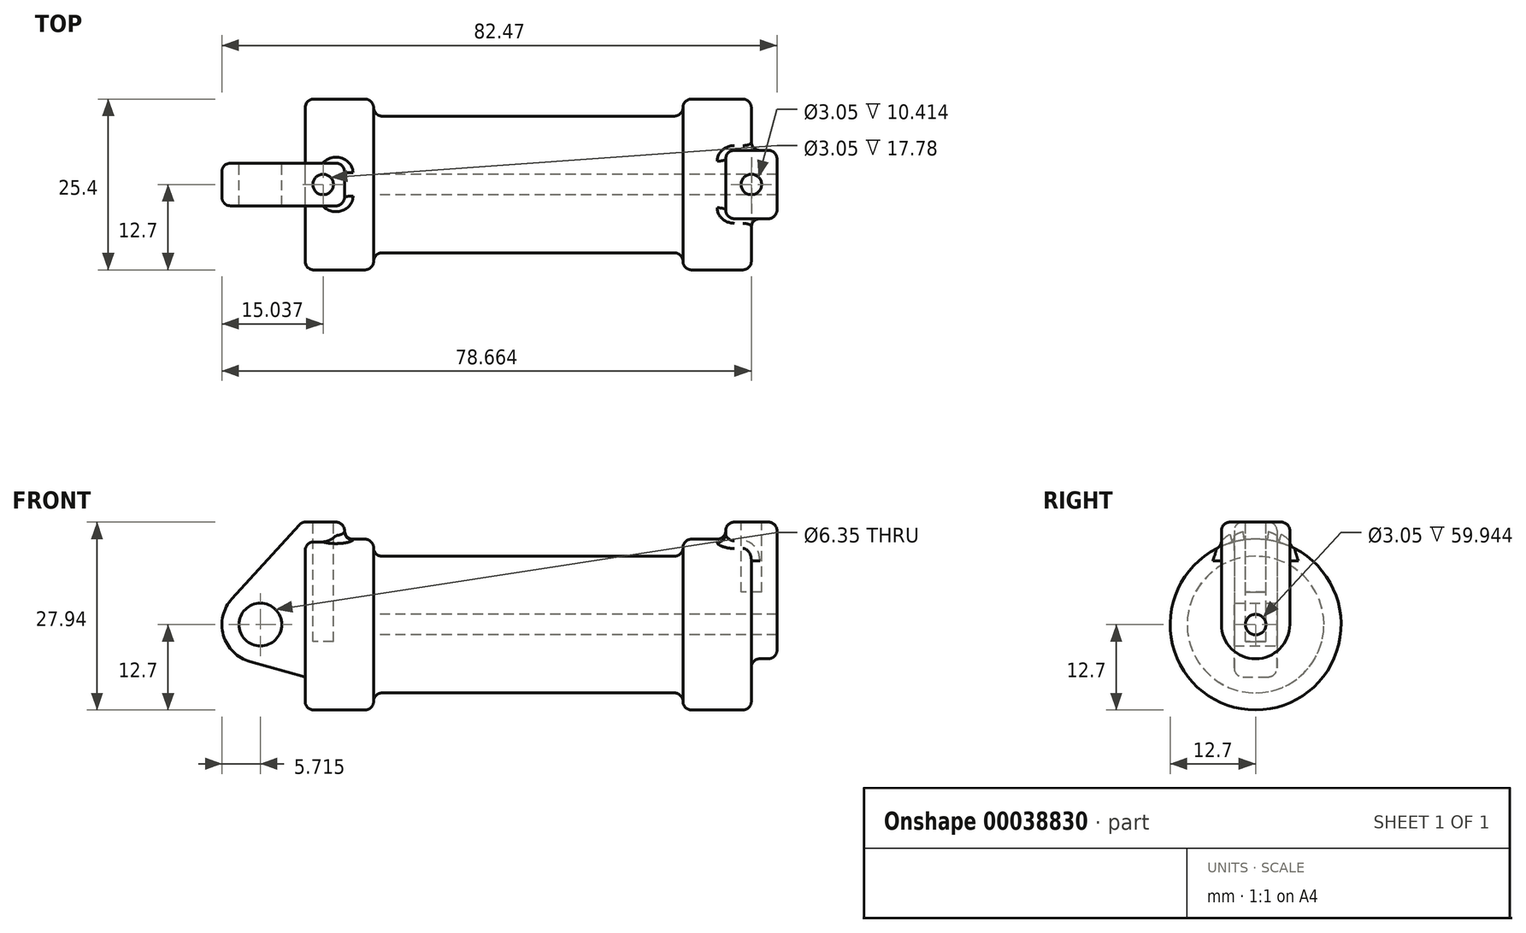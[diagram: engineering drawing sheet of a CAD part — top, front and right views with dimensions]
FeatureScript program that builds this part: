
annotation { "Feature Type Name" : "Feature", "Feature Type Description" : "" }
export const myFeature = defineFeature(function(context is Context, id is Id, definition is map)
    precondition{}
    {
        {
            var Q0;
            Q0=qCreatedBy(makeId("Front.planeOp"),FACE);
            var sketch = newSketch(context, id + "F0", { "sketchPlane" : qUnion([Q0])});
            skLineSegment(sketch, "E0", {"start": v(0, 0) * mm, "end": v(0, 12.7) * mm});
            skLineSegment(sketch, "E1", {"start": v(0, 12.7) * mm, "end": v(10.16, 12.7) * mm});
            skLineSegment(sketch, "E2", {"start": v(10.16, 12.7) * mm, "end": v(10.16, 10.16) * mm});
            skLineSegment(sketch, "E3", {"start": v(10.16, 10.16) * mm, "end": v(56.13, 10.16) * mm});
            skLineSegment(sketch, "E4", {"start": v(56.13, 10.16) * mm, "end": v(56.13, 12.7) * mm});
            skLineSegment(sketch, "E5", {"start": v(56.13, 12.7) * mm, "end": v(66.3, 12.7) * mm});
            skLineSegment(sketch, "E6", {"start": v(66.3, 12.7) * mm, "end": v(66.3, 0) * mm});
            skLineSegment(sketch, "E7", {"start": v(66.3, 0) * mm, "end": v(0, 0) * mm});
            skLineSegment(sketch, "E8", {"start": v(5.84, 15.24) * mm, "end": v(-0.5, 15.24) * mm});
            skLineSegment(sketch, "E9", {"start": v(-0.5, 15.24) * mm, "end": v(-10.88, 3.85) * mm});
            skLineSegment(sketch, "E10", {"start": v(0, 0) * mm, "end": v(-6.65, 0) * mm});
            skCircle(sketch, "E11", {"center": v(-6.65, 0) * mm, "radius": 5.72 * mm});
            skCircle(sketch, "E12", {"center": v(-6.65, 0) * mm, "radius": 3.18 * mm});
            skLineSegment(sketch, "E13", {"start": v(5.84, 15.24) * mm, "end": v(5.84, -9.4) * mm});
            skLineSegment(sketch, "E14", {"start": v(5.84, -9.4) * mm, "end": v(-8.18, -5.5) * mm});
            skSolve(sketch);
        }
        {
            var Q0;
            {var subQ6=sQuery(id+"F0.wireOp",EDGE,"E2");Q0=makeQuery(id+"F0.imprint","IMPRINT",FACE,{"disambiguationData":[TD([[makeQuery(id+"F0.imprint","IMPRINT",EDGE,{"derivedFrom":subQ6}),-1.0]])]});}
            var Q1;
            {var subQ5=sQuery(id+"F0.wireOp",EDGE,"E0");Q1=makeQuery(id+"F0.imprint","IMPRINT",FACE,{"disambiguationData":[TD([[makeQuery(id+"F0.imprint","IMPRINT",EDGE,{"derivedFrom":subQ5}),-1.0]])]});}
            var Q2;
            Q2=sQuery(id+"F0.wireOp",EDGE,"E7");
            revolve(context, id + "F1", {"entities" : qUnion([Q0, Q1]), "axis" : qUnion([Q2]), "revolveType" : RevolveType.FULL});
        }
        {
            var Q0;
            {var subQ0=sQuery(id+"F0.wireOp",EDGE,"E14");Q0=makeQuery(id+"F0.imprint","IMPRINT",FACE,{"disambiguationData":[TD([[makeQuery(id+"F0.imprint","IMPRINT",EDGE,{"derivedFrom":subQ0}),-1.0]])]});}
            var Q1;
            {var subQ0=sQuery(id+"F0.wireOp",EDGE,"E12");Q1=makeQuery(id+"F0.imprint","IMPRINT",FACE,{"disambiguationData":[TD([[makeQuery(id+"F0.imprint","IMPRINT",EDGE,{"derivedFrom":subQ0}),-1.0]])]});}
            var Q2;
            {var subQ8=sQuery(id+"F0.wireOp",EDGE,"E0");Q2=makeQuery(id+"F0.imprint","IMPRINT",FACE,{"disambiguationData":[TD([[makeQuery(id+"F0.imprint","IMPRINT",EDGE,{"derivedFrom":subQ8}),1.0]])]});}
            var Q3;
            {var subQ5=sQuery(id+"F0.wireOp",EDGE,"E0");Q3=makeQuery(id+"F0.imprint","IMPRINT",FACE,{"disambiguationData":[TD([[makeQuery(id+"F0.imprint","IMPRINT",EDGE,{"derivedFrom":subQ5}),-1.0]])]});}
            extrude(context, id + "F2", {"entities" : qUnion([Q0, Q1, Q2, Q3]), "operationType" : NewBodyOperationType.ADD, "endBound" : BoundingType.SYMMETRIC, "depth" : 6.35 * mm});
        }
        {
            var Q0;
            Q0=makeQuery(id+"F1.opRevolve","SWEPT_FACE",FACE,{"disambiguationData":[OSD([sQuery(id+"F0.wireOp",EDGE,"E6")])]});
            var sketch = newSketch(context, id + "F3", { "sketchPlane" : qUnion([Q0])});
            skCircle(sketch, "E15", {"center": v(0, 0) * mm, "radius": 1.52 * mm});
            skCircle(sketch, "E16", {"center": v(0, 0) * mm, "radius": 5.08 * mm});
            skLineSegment(sketch, "E17", {"start": v(-5.08, 0) * mm, "end": v(-5.08, 15.24) * mm});
            skLineSegment(sketch, "E18", {"start": v(-5.08, 15.24) * mm, "end": v(5.08, 15.24) * mm});
            skLineSegment(sketch, "E19", {"start": v(5.08, 15.24) * mm, "end": v(5.08, 0) * mm});
            skSolve(sketch);
        }
        {
            var Q0;
            Q0=makeQuery(id+"F3.imprint","IMPRINT",FACE,{"disambiguationData":[TD([[makeQuery(id+"F3.imprint","IMPRINT",EDGE,{"derivedFrom":sQuery(id+"F3.wireOp",EDGE,"E15")}),-1.0]])]});
            var Q1;
            {var subQ3=sQuery(id+"F3.wireOp",EDGE,"E17");var subQ5=sQuery(id+"F3.wireOp",EDGE,"E16");var subQ7=makeQuery(id+"F3.imprint","INTERSECT",VERTEX,{"derivedFrom":[subQ5,subQ3]});Q1=makeQuery(id+"F3.imprint","IMPRINT",FACE,{"disambiguationData":[TD([[makeQuery(id+"F3.imprint","IMPRINT",EDGE,{"disambiguationData":[TD([[subQ7,1.0]])],"derivedFrom":subQ5}),-1.0]])]});}
            var Q2;
            {var subQ5=sQuery(id+"F3.wireOp",EDGE,"E18");Q2=makeQuery(id+"F3.imprint","IMPRINT",FACE,{"disambiguationData":[TD([[makeQuery(id+"F3.imprint","IMPRINT",EDGE,{"derivedFrom":subQ5}),-1.0]])]});}
            extrude(context, id + "F4", {"entities" : qUnion([Q0, Q1, Q2]), "operationType" : NewBodyOperationType.ADD, "endBound" : BoundingType.SYMMETRIC, "depth" : 7.62 * mm});
        }
        {
            var Q0;
            Q0=makeQuery(id+"F4.boolean.opBoolean","SPLIT",FACE,{"disambiguationData":[TD([makeQuery(id+"F4.opExtrude","SWEPT_FACE",FACE,{"disambiguationData":[OSD([sQuery(id+"F3.wireOp",EDGE,"E15")])]})])],"derivedFrom":makeQuery(id+"F1.opRevolve","SWEPT_FACE",FACE,{"disambiguationData":[OSD([sQuery(id+"F0.wireOp",EDGE,"E6")])]})});
            var Q1;
            Q1=makeQuery(id+"F1.opRevolve","SWEPT_FACE",FACE,{"disambiguationData":[OSD([sQuery(id+"F0.wireOp",EDGE,"E2")])]});
            extrude(context, id + "F5", {"entities" : qUnion([Q0]), "operationType" : NewBodyOperationType.REMOVE, "endBound" : BoundingType.UP_TO_SURFACE, "oppositeDirection" : true, "endBoundEntityFace" : qUnion([Q1]), "depth" : 25.4 * mm});
        }
        {
            var Q0;
            Q0=makeQuery(id+"F4.opExtrude","SWEPT_FACE",FACE,{"disambiguationData":[OSD([sQuery(id+"F3.wireOp",EDGE,"E18")])]});
            var sketch = newSketch(context, id + "F6", { "sketchPlane" : qUnion([Q0])});
            skLineSegment(sketch, "E20", {"start": v(66.3, 5.08) * mm, "end": v(66.3, -5.08) * mm, "construction": true});
            skLineSegment(sketch, "E21", {"start": v(62.48, 0) * mm, "end": v(70.1, 0) * mm, "construction": true});
            skCircle(sketch, "E22", {"center": v(66.3, 0) * mm, "radius": 1.52 * mm});
            skLineSegment(sketch, "E23", {"start": v(2.6, 3.14) * mm, "end": v(2.6, -3.16) * mm, "construction": true});
            skLineSegment(sketch, "E24", {"start": v(-0.52, 0) * mm, "end": v(5.82, 0) * mm, "construction": true});
            skSolve(sketch);
        }
        {
            var Q0;
            Q0=makeQuery(id+"F2.opExtrude","SWEPT_FACE",FACE,{"disambiguationData":[OSD([sQuery(id+"F0.wireOp",EDGE,"E8")])]});
            var sketch = newSketch(context, id + "F7", { "sketchPlane" : qUnion([Q0])});
            skLineSegment(sketch, "E25", {"start": v(2.67, 3.18) * mm, "end": v(2.67, -3.18) * mm, "construction": true});
            skLineSegment(sketch, "E26", {"start": v(-0.5, 0) * mm, "end": v(5.84, 0) * mm, "construction": true});
            skCircle(sketch, "E27", {"center": v(2.67, 0) * mm, "radius": 1.52 * mm});
            skSolve(sketch);
        }
        {
            var Q0;
            Q0=makeQuery(id+"F6.imprint","IMPRINT",FACE,{"disambiguationData":[TD([[makeQuery(id+"F6.imprint","IMPRINT",EDGE,{"derivedFrom":sQuery(id+"F6.wireOp",EDGE,"E22")}),1.0]])]});
            extrude(context, id + "F8", {"entities" : qUnion([Q0]), "operationType" : NewBodyOperationType.REMOVE, "oppositeDirection" : true, "depth" : 10.4 * mm});
        }
        {
            var Q0;
            Q0=makeQuery(id+"F7.imprint","IMPRINT",FACE,{"disambiguationData":[TD([[makeQuery(id+"F7.imprint","IMPRINT",EDGE,{"derivedFrom":sQuery(id+"F7.wireOp",EDGE,"E27")}),1.0]])]});
            extrude(context, id + "F9", {"entities" : qUnion([Q0]), "operationType" : NewBodyOperationType.REMOVE, "oppositeDirection" : true, "depth" : 17.78 * mm});
        }
        {
            var Q0;
            Q0=makeQuery(id+"F1.opRevolve","SWEPT_EDGE",EDGE,{"disambiguationData":[OSD([sQuery(id+"F0.wireOp",EDGE,"E1"),sQuery(id+"F0.wireOp",EDGE,"E2")])]});
            var Q1;
            Q1=makeQuery(id+"F1.opRevolve","SWEPT_EDGE",EDGE,{"disambiguationData":[OSD([sQuery(id+"F0.wireOp",EDGE,"E2"),sQuery(id+"F0.wireOp",EDGE,"E3")])]});
            var Q2;
            Q2=makeQuery(id+"F1.opRevolve","SWEPT_EDGE",EDGE,{"disambiguationData":[OSD([sQuery(id+"F0.wireOp",EDGE,"E0"),sQuery(id+"F0.wireOp",EDGE,"E1")])]});
            var Q3;
            Q3=makeQuery(id+"F1.opRevolve","SWEPT_EDGE",EDGE,{"disambiguationData":[OSD([sQuery(id+"F0.wireOp",EDGE,"E5"),sQuery(id+"F0.wireOp",EDGE,"E6")])]});
            var Q4;
            Q4=makeQuery(id+"F1.opRevolve","SWEPT_EDGE",EDGE,{"disambiguationData":[OSD([sQuery(id+"F0.wireOp",EDGE,"E4"),sQuery(id+"F0.wireOp",EDGE,"E5")])]});
            var Q5;
            Q5=makeQuery(id+"F1.opRevolve","SWEPT_EDGE",EDGE,{"disambiguationData":[OSD([sQuery(id+"F0.wireOp",EDGE,"E3"),sQuery(id+"F0.wireOp",EDGE,"E4")])]});
            fillet(context, id + "F10", {"entities" : qUnion([Q0, Q1, Q2, Q3, Q4, Q5]), "radius" : 1.27 * mm, "tangentPropagation" : true, "allowEdgeOverflow" : false});
        }
        {
            var Q0;
            Q0=makeQuery(id+"F2.boolean.opBoolean","INTERSECT",EDGE,{"derivedFrom":[makeQuery(id+"F1.opRevolve","SWEPT_FACE",FACE,{"disambiguationData":[OSD([sQuery(id+"F0.wireOp",EDGE,"E1")])]}),makeQuery(id+"F2.opExtrude","SWEPT_FACE",FACE,{"disambiguationData":[OSD([sQuery(id+"F0.wireOp",EDGE,"E13")])]})]});
            var Q1;
            Q1=makeQuery(id+"F2.opExtrude","CAP_EDGE",EDGE,{"disambiguationData":[OSD([sQuery(id+"F0.wireOp",EDGE,"E13")])],"isStart":false});
            var Q2;
            Q2=makeQuery(id+"F2.opExtrude","CAP_EDGE",EDGE,{"disambiguationData":[OSD([sQuery(id+"F0.wireOp",EDGE,"E13")])],"isStart":true});
            var Q3;
            Q3=makeQuery(id+"F2.opExtrude","CAP_EDGE",EDGE,{"disambiguationData":[OSD([sQuery(id+"F0.wireOp",EDGE,"E8")])],"isStart":false});
            var Q4;
            Q4=makeQuery(id+"F2.opExtrude","SWEPT_EDGE",EDGE,{"disambiguationData":[OSD([sQuery(id+"F0.wireOp",EDGE,"E8"),sQuery(id+"F0.wireOp",EDGE,"E9")])]});
            var Q5;
            Q5=makeQuery(id+"F2.opExtrude","CAP_EDGE",EDGE,{"disambiguationData":[OSD([sQuery(id+"F0.wireOp",EDGE,"E8")])],"isStart":true});
            var Q6;
            Q6=makeQuery(id+"F2.opExtrude","SWEPT_EDGE",EDGE,{"disambiguationData":[OSD([sQuery(id+"F0.wireOp",EDGE,"E8"),sQuery(id+"F0.wireOp",EDGE,"E13")])]});
            var Q7;
            Q7=makeQuery(id+"F2.opExtrude","CAP_EDGE",EDGE,{"disambiguationData":[OSD([sQuery(id+"F0.wireOp",EDGE,"E14")])],"isStart":false});
            var Q8;
            Q8=makeQuery(id+"F2.opExtrude","CAP_EDGE",EDGE,{"disambiguationData":[OSD([sQuery(id+"F0.wireOp",EDGE,"E11")])],"isStart":false});
            var Q9;
            Q9=makeQuery(id+"F2.opExtrude","CAP_EDGE",EDGE,{"disambiguationData":[OSD([sQuery(id+"F0.wireOp",EDGE,"E9")])],"isStart":false});
            var Q10;
            Q10=makeQuery(id+"F2.opExtrude","CAP_EDGE",EDGE,{"disambiguationData":[OSD([sQuery(id+"F0.wireOp",EDGE,"E9")])],"isStart":true});
            var Q11;
            Q11=makeQuery(id+"F2.opExtrude","CAP_EDGE",EDGE,{"disambiguationData":[OSD([sQuery(id+"F0.wireOp",EDGE,"E11")])],"isStart":true});
            var Q12;
            Q12=makeQuery(id+"F2.opExtrude","CAP_EDGE",EDGE,{"disambiguationData":[OSD([sQuery(id+"F0.wireOp",EDGE,"E14")])],"isStart":true});
            fillet(context, id + "F11", {"entities" : qUnion([Q0, Q1, Q2, Q3, Q4, Q5, Q6, Q7, Q8, Q9, Q10, Q11, Q12]), "radius" : 1.27 * mm, "tangentPropagation" : true, "allowEdgeOverflow" : false});
        }
        {
            var Q0;
            Q0=makeQuery(id+"F4.opExtrude","CAP_EDGE",EDGE,{"disambiguationData":[OSD([sQuery(id+"F3.wireOp",EDGE,"E18")])],"isStart":true});
            var Q1;
            Q1=makeQuery(id+"F4.boolean.opBoolean","INTERSECT",EDGE,{"derivedFrom":[makeQuery(id+"F1.opRevolve","SWEPT_FACE",FACE,{"disambiguationData":[OSD([sQuery(id+"F0.wireOp",EDGE,"E5")])]}),makeQuery(id+"F4.opExtrude","CAP_FACE",FACE,{"disambiguationData":[OSD([sQuery(id+"F3.wireOp",EDGE,"E15"),sQuery(id+"F3.wireOp",EDGE,"E16"),sQuery(id+"F3.wireOp",EDGE,"E17"),sQuery(id+"F3.wireOp",EDGE,"E18"),sQuery(id+"F3.wireOp",EDGE,"E19")])],"isStart":true})]});
            var Q2;
            Q2=makeQuery(id+"F4.opExtrude","SWEPT_EDGE",EDGE,{"disambiguationData":[OSD([sQuery(id+"F3.wireOp",EDGE,"E17"),sQuery(id+"F3.wireOp",EDGE,"E18")])]});
            var Q3;
            Q3=makeQuery(id+"F4.opExtrude","CAP_EDGE",EDGE,{"disambiguationData":[OSD([sQuery(id+"F3.wireOp",EDGE,"E17")])],"isStart":true});
            var Q4;
            Q4=makeQuery(id+"F4.opExtrude","CAP_EDGE",EDGE,{"disambiguationData":[OSD([sQuery(id+"F3.wireOp",EDGE,"E17")])],"isStart":false});
            var Q5;
            Q5=makeQuery(id+"F4.opExtrude","SWEPT_EDGE",EDGE,{"disambiguationData":[OSD([sQuery(id+"F3.wireOp",EDGE,"E18"),sQuery(id+"F3.wireOp",EDGE,"E19")])]});
            var Q6;
            Q6=makeQuery(id+"F4.opExtrude","CAP_EDGE",EDGE,{"disambiguationData":[OSD([sQuery(id+"F3.wireOp",EDGE,"E18")])],"isStart":false});
            var Q7;
            Q7=makeQuery(id+"F4.opExtrude","CAP_EDGE",EDGE,{"disambiguationData":[OSD([sQuery(id+"F3.wireOp",EDGE,"E19")])],"isStart":true});
            var Q8;
            Q8=makeQuery(id+"F4.opExtrude","CAP_EDGE",EDGE,{"disambiguationData":[OSD([sQuery(id+"F3.wireOp",EDGE,"E19")])],"isStart":false});
            var Q9;
            Q9=makeQuery(id+"F4.boolean.opBoolean","INTERSECT",EDGE,{"derivedFrom":[makeQuery(id+"F1.opRevolve","SWEPT_FACE",FACE,{"disambiguationData":[OSD([sQuery(id+"F0.wireOp",EDGE,"E6")])]}),makeQuery(id+"F4.opExtrude","SWEPT_FACE",FACE,{"disambiguationData":[OSD([sQuery(id+"F3.wireOp",EDGE,"E19")])]})]});
            var Q10;
            Q10=makeQuery(id+"F10.opFillet","BLEND_EDGE",EDGE,{"blendedFrom":[makeQuery(id+"F1.opRevolve","SWEPT_EDGE",EDGE,{"disambiguationData":[OSD([sQuery(id+"F0.wireOp",EDGE,"E5"),sQuery(id+"F0.wireOp",EDGE,"E6")])]}),makeQuery(id+"F4.opExtrude","SWEPT_FACE",FACE,{"disambiguationData":[OSD([sQuery(id+"F3.wireOp",EDGE,"E19")])]})],"blendedInto":[makeQuery(id+"F4.opExtrude","SWEPT_FACE",FACE,{"disambiguationData":[OSD([sQuery(id+"F3.wireOp",EDGE,"E19")])]})]});
            var Q11;
            Q11=makeQuery(id+"F4.boolean.opBoolean","INTERSECT",EDGE,{"derivedFrom":[makeQuery(id+"F1.opRevolve","SWEPT_FACE",FACE,{"disambiguationData":[OSD([sQuery(id+"F0.wireOp",EDGE,"E5")])]}),makeQuery(id+"F4.opExtrude","SWEPT_FACE",FACE,{"disambiguationData":[OSD([sQuery(id+"F3.wireOp",EDGE,"E19")])]})]});
            var Q12;
            Q12=makeQuery(id+"F4.opExtrude","CAP_EDGE",EDGE,{"disambiguationData":[OSD([sQuery(id+"F3.wireOp",EDGE,"E16")])],"isStart":false});
            var Q13;
            Q13=makeQuery(id+"F4.boolean.opBoolean","INTERSECT",EDGE,{"derivedFrom":[makeQuery(id+"F1.opRevolve","SWEPT_FACE",FACE,{"disambiguationData":[OSD([sQuery(id+"F0.wireOp",EDGE,"E6")])]}),makeQuery(id+"F4.opExtrude","SWEPT_FACE",FACE,{"disambiguationData":[OSD([sQuery(id+"F3.wireOp",EDGE,"E16")])]})]});
            var Q14;
            Q14=makeQuery(id+"F4.boolean.opBoolean","INTERSECT",EDGE,{"derivedFrom":[makeQuery(id+"F1.opRevolve","SWEPT_FACE",FACE,{"disambiguationData":[OSD([sQuery(id+"F0.wireOp",EDGE,"E6")])]}),makeQuery(id+"F4.opExtrude","SWEPT_FACE",FACE,{"disambiguationData":[OSD([sQuery(id+"F3.wireOp",EDGE,"E17")])]})]});
            var Q15;
            Q15=makeQuery(id+"F10.opFillet","BLEND_EDGE",EDGE,{"blendedFrom":[makeQuery(id+"F1.opRevolve","SWEPT_EDGE",EDGE,{"disambiguationData":[OSD([sQuery(id+"F0.wireOp",EDGE,"E5"),sQuery(id+"F0.wireOp",EDGE,"E6")])]}),makeQuery(id+"F4.opExtrude","SWEPT_FACE",FACE,{"disambiguationData":[OSD([sQuery(id+"F3.wireOp",EDGE,"E17")])]})],"blendedInto":[makeQuery(id+"F4.opExtrude","SWEPT_FACE",FACE,{"disambiguationData":[OSD([sQuery(id+"F3.wireOp",EDGE,"E17")])]})]});
            var Q16;
            Q16=makeQuery(id+"F4.boolean.opBoolean","INTERSECT",EDGE,{"derivedFrom":[makeQuery(id+"F1.opRevolve","SWEPT_FACE",FACE,{"disambiguationData":[OSD([sQuery(id+"F0.wireOp",EDGE,"E5")])]}),makeQuery(id+"F4.opExtrude","SWEPT_FACE",FACE,{"disambiguationData":[OSD([sQuery(id+"F3.wireOp",EDGE,"E17")])]})]});
            fillet(context, id + "F12", {"entities" : qUnion([Q0, Q1, Q2, Q3, Q4, Q5, Q6, Q7, Q8, Q9, Q10, Q11, Q12, Q13, Q14, Q15, Q16]), "radius" : 1.27 * mm, "tangentPropagation" : true, "allowEdgeOverflow" : false});
        }
    });
